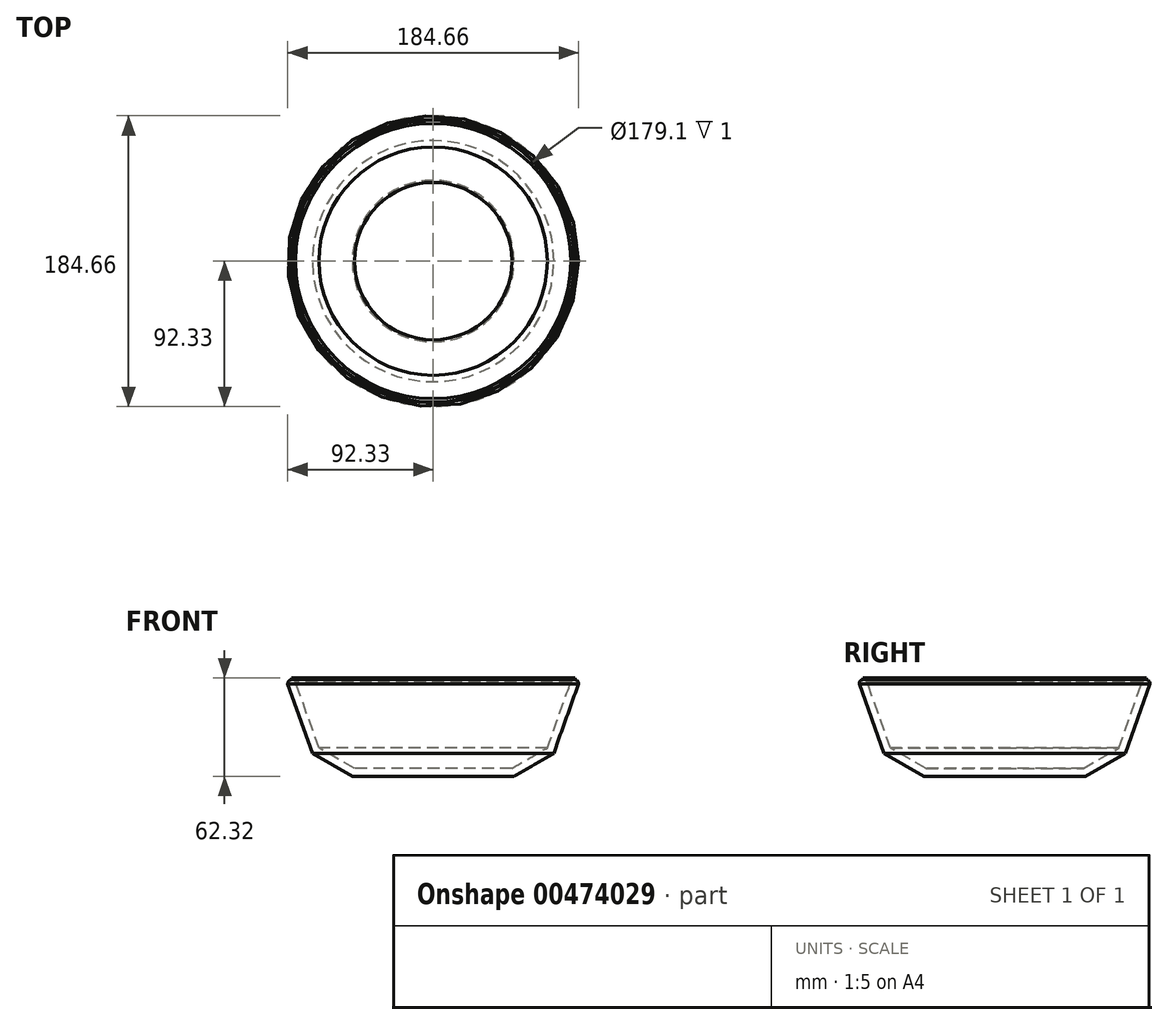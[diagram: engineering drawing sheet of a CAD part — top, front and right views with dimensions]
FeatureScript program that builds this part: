
annotation { "Feature Type Name" : "Feature", "Feature Type Description" : "" }
export const myFeature = defineFeature(function(context is Context, id is Id, definition is map)
    precondition{}
    {
        {
            var Q0;
            Q0=qCreatedBy(makeId("Front.planeOp"),FACE);
            var sketch = newSketch(context, id + "F0", { "sketchPlane" : qUnion([Q0])});
            skLineSegment(sketch, "E0", {"start": v(0, -15) * mm, "end": v(50, -15) * mm});
            skLineSegment(sketch, "E1", {"start": v(50, -15) * mm, "end": v(72.52, -2) * mm});
            skPoint(sketch, "E2", {"position": v(53.43, 0) * mm});
            skLineSegment(sketch, "E3", {"start": v(72.52, -2) * mm, "end": v(87.43, 39.75) * mm});
            skLineSegment(sketch, "E4.0", {"start": v(76.6, -5.41) * mm, "end": v(92.32, 38.59) * mm});
            skLineSegment(sketch, "E4.1", {"start": v(51.34, -20) * mm, "end": v(76.6, -5.41) * mm});
            skLineSegment(sketch, "E4.2", {"start": v(0, -20) * mm, "end": v(51.34, -20) * mm});
            skLineSegment(sketch, "E5", {"start": v(90.02, 41.32) * mm, "end": v(89.55, 41.32) * mm});
            skArc(sketch, "E6", {"start": v(92.32, 38.59) * mm, "mid": v(90.26, 41.28) * mm, "end": v(87.35, 39.53) * mm});
            skPoint(sketch, "E6.first.point", {"position": v(87.43, 39.75) * mm});
            skPoint(sketch, "E6.second.point", {"position": v(92.32, 38.59) * mm});
            skPoint(sketch, "E6.third.point", {"position": v(90.02, 41.32) * mm});
            skLineSegment(sketch, "E7", {"start": v(0, -15) * mm, "end": v(0, -20) * mm});
            skSolve(sketch);
        }
        {
            var Q0;
            Q0=makeQuery(id+"F0.imprint","IMPRINT",FACE,{"disambiguationData":[TD([[makeQuery(id+"F0.imprint","IMPRINT",EDGE,{"derivedFrom":sQuery(id+"F0.wireOp",EDGE,"E0")}),-1.0]])]});
            var Q1;
            Q1=sQuery(id+"F0.wireOp",EDGE,"E7");
            revolve(context, id + "F1", {"entities" : qUnion([Q0]), "axis" : qUnion([Q1]), "revolveType" : RevolveType.FULL});
        }
        {
            var Q0;
            Q0=makeQuery(id+"F1.opRevolve","SWEPT_FACE",FACE,{"disambiguationData":[OSD([sQuery(id+"F0.wireOp",EDGE,"E5")])]});
            extrude(context, id + "F2", {"entities" : qUnion([Q0]), "operationType" : NewBodyOperationType.ADD, "depth" : 1 * mm});
        }
    });
